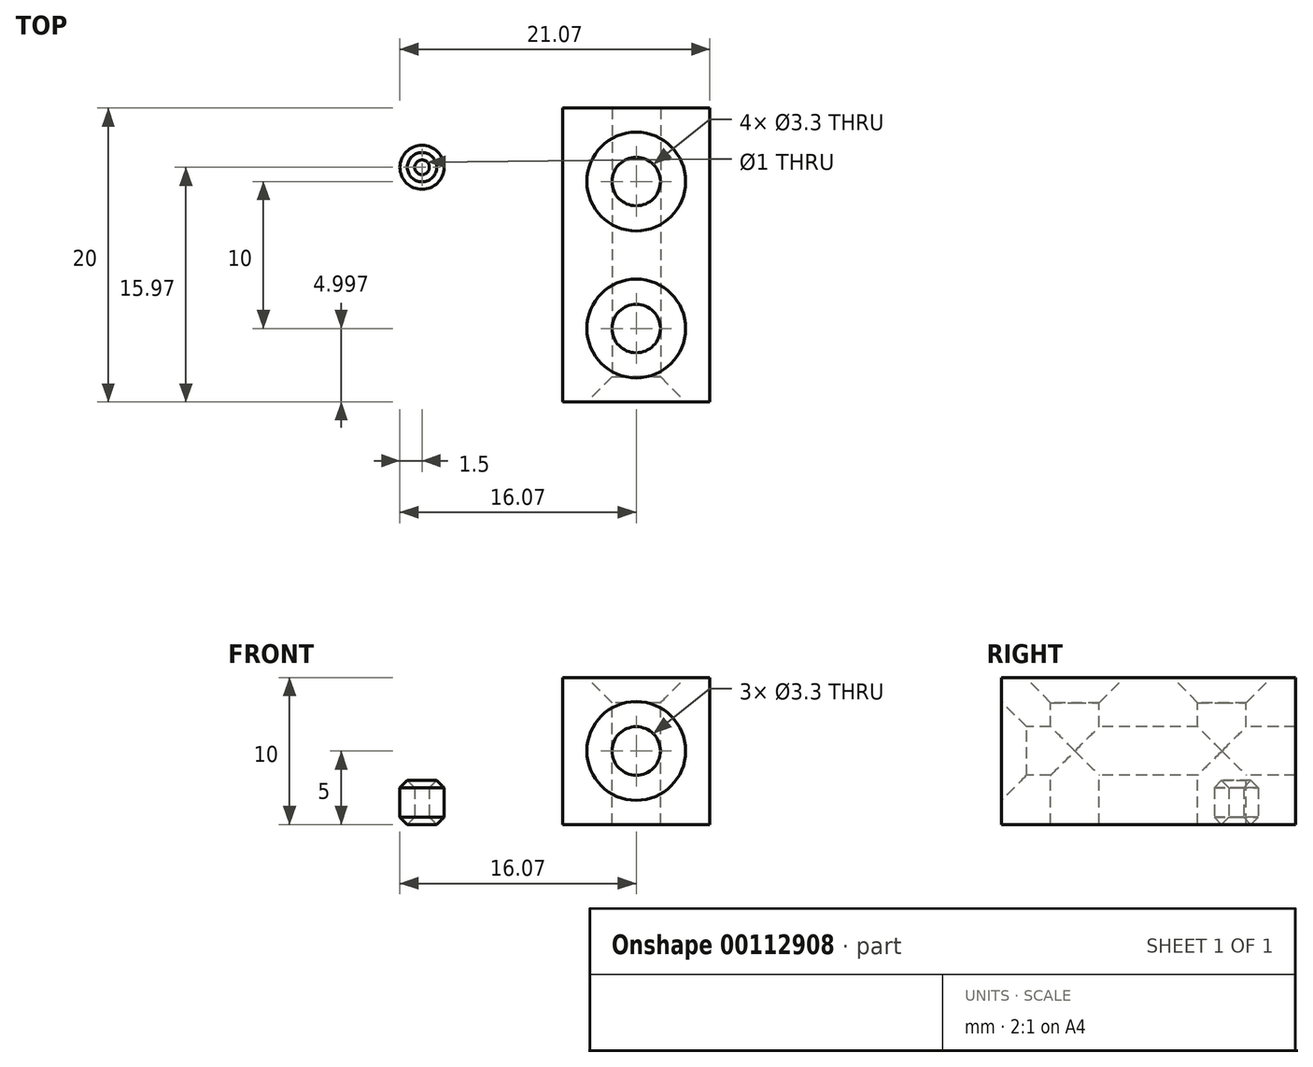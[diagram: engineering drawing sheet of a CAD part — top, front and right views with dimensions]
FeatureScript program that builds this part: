
annotation { "Feature Type Name" : "Feature", "Feature Type Description" : "" }
export const myFeature = defineFeature(function(context is Context, id is Id, definition is map)
    precondition{}
    {
        {
            assignVariable(context, id + "F0", {"name" : "X", "anyValue" : 10});
        }
        {
            var Q0;
            Q0=qCreatedBy(makeId("Top.planeOp"),FACE);
            var sketch = newSketch(context, id + "F1", { "sketchPlane" : qUnion([Q0])});
            skCircle(sketch, "E0", {"center": v(0, 0) * mm, "radius": 1.5 * mm});
            skCircle(sketch, "E1", {"center": v(0, 0) * mm, "radius": 0.5 * mm});
            skSolve(sketch);
        }
        {
            var Q0;
            Q0 = qSketchRegion(id + "F1", true);
            extrude(context, id + "F2", {"entities" : qUnion([Q0]), "depth" : 3 * mm});
        }
        {
            var Q0;
            Q0=makeQuery(id+"F2.opExtrude","CAP_EDGE",EDGE,{"disambiguationData":[OSD([sQuery(id+"F1.wireOp",EDGE,"E1")])],"isStart":false});
            var Q1;
            Q1=makeQuery(id+"F2.opExtrude","CAP_EDGE",EDGE,{"disambiguationData":[OSD([sQuery(id+"F1.wireOp",EDGE,"E0")])],"isStart":false});
            var Q2;
            Q2=makeQuery(id+"F2.opExtrude","CAP_EDGE",EDGE,{"disambiguationData":[OSD([sQuery(id+"F1.wireOp",EDGE,"E0")])],"isStart":true});
            var Q3;
            Q3=makeQuery(id+"F2.opExtrude","CAP_EDGE",EDGE,{"disambiguationData":[OSD([sQuery(id+"F1.wireOp",EDGE,"E1")])],"isStart":true});
            chamfer(context, id + "F3", {"entities" : qUnion([Q0, Q1, Q2, Q3]), "width" : .5 * mm, "tangentPropagation" : true});
        }
        {
            var Q0;
            Q0=qCreatedBy(makeId("Top.planeOp"),FACE);
            var sketch = newSketch(context, id + "F4", { "sketchPlane" : qUnion([Q0])});
            skLineSegment(sketch, "E2.bottom", {"start": v(9.57, 4.03) * mm, "end": v(19.57, 4.03) * mm});
            skLineSegment(sketch, "E2.top", {"start": v(9.57, -15.97) * mm, "end": v(19.57, -15.97) * mm});
            skLineSegment(sketch, "E2.left", {"start": v(9.57, 4.03) * mm, "end": v(9.57, -15.97) * mm});
            skLineSegment(sketch, "E2.right", {"start": v(19.57, 4.03) * mm, "end": v(19.57, -15.97) * mm});
            skSolve(sketch);
        }
        {
            var Q0;
            Q0=makeQuery(id+"F4.imprint","IMPRINT",FACE,{"disambiguationData":[TD([[makeQuery(id+"F4.imprint","IMPRINT",EDGE,{"derivedFrom":sQuery(id+"F4.wireOp",EDGE,"E2.bottom")}),-1.0]])]});
            extrude(context, id + "F5", {"entities" : qUnion([Q0]), "depth" : (getVariable(context, 'X')) * mm});
        }
        {
            var Q0;
            Q0=makeQuery(id+"F5.opExtrude","SWEPT_FACE",FACE,{"disambiguationData":[OSD([sQuery(id+"F4.wireOp",EDGE,"E2.top")])]});
            var sketch = newSketch(context, id + "F6", { "sketchPlane" : qUnion([Q0])});
            skPoint(sketch, "E3", {"position": v(14.57, 5) * mm});
            skSolve(sketch);
        }
        {
            var Q0;
            Q0=sQuery(id+"F6.wireOp",VERTEX,"E3");
            var Q1;
            Q1=makeQuery(id+"F5.opExtrude","SWEPT_BODY",BODY,{"disambiguationData":[OSD([sQuery(id+"F4.wireOp",EDGE,"E2.bottom"),sQuery(id+"F4.wireOp",EDGE,"E2.top"),sQuery(id+"F4.wireOp",EDGE,"E2.left"),sQuery(id+"F4.wireOp",EDGE,"E2.right")])]});
            hole(context, id + "F7", {"style" : HoleStyle.C_SINK, "endStyle" : HoleEndStyle.THROUGH, "standardTappedOrClearance" : lookupTablePath({ "standard" : "ISO", "fit" : "Normal", "size" : "M3", "type" : "Clearance" }), "standardBlindInLast" : lookupTablePath({ "fit" : "Standard", "standard" : "ISO", "size" : "M3", "type" : "Clearance" }), "holeDiameter" : 3.3 * mm, "cSinkDiameter" : 6.72 * mm, "cSinkAngle" : 90 * degree, "locations" : qUnion([Q0]), "scope" : qUnion([Q1]), "isTappedThrough" : true});
        }
        {
            var Q0;
            Q0=makeQuery(id+"F5.opExtrude","CAP_FACE",FACE,{"disambiguationData":[OSD([sQuery(id+"F4.wireOp",EDGE,"E2.bottom"),sQuery(id+"F4.wireOp",EDGE,"E2.top"),sQuery(id+"F4.wireOp",EDGE,"E2.left"),sQuery(id+"F4.wireOp",EDGE,"E2.right")])],"isStart":false});
            var sketch = newSketch(context, id + "F8", { "sketchPlane" : qUnion([Q0])});
            skPoint(sketch, "E4", {"position": v(14.57, -10.97) * mm});
            skPoint(sketch, "E5", {"position": v(14.57, -0.97) * mm});
            skSolve(sketch);
        }
        {
            var Q0;
            Q0=sQuery(id+"F8.wireOp",VERTEX,"E4");
            var Q1;
            Q1=sQuery(id+"F8.wireOp",VERTEX,"E5");
            var Q2;
            Q2=makeQuery(id+"F5.opExtrude","SWEPT_BODY",BODY,{"disambiguationData":[OSD([sQuery(id+"F4.wireOp",EDGE,"E2.bottom"),sQuery(id+"F4.wireOp",EDGE,"E2.top"),sQuery(id+"F4.wireOp",EDGE,"E2.left"),sQuery(id+"F4.wireOp",EDGE,"E2.right")])]});
            hole(context, id + "F9", {"style" : HoleStyle.C_SINK, "endStyle" : HoleEndStyle.THROUGH, "standardTappedOrClearance" : lookupTablePath({ "standard" : "ISO", "fit" : "Normal", "size" : "M3", "type" : "Clearance" }), "standardBlindInLast" : lookupTablePath({ "fit" : "Standard", "standard" : "ISO", "size" : "M3", "type" : "Clearance" }), "holeDiameter" : 3.3 * mm, "cSinkDiameter" : 6.72 * mm, "cSinkAngle" : 90 * degree, "locations" : qUnion([Q0, Q1]), "scope" : qUnion([Q2]), "isTappedThrough" : true});
        }
    });
